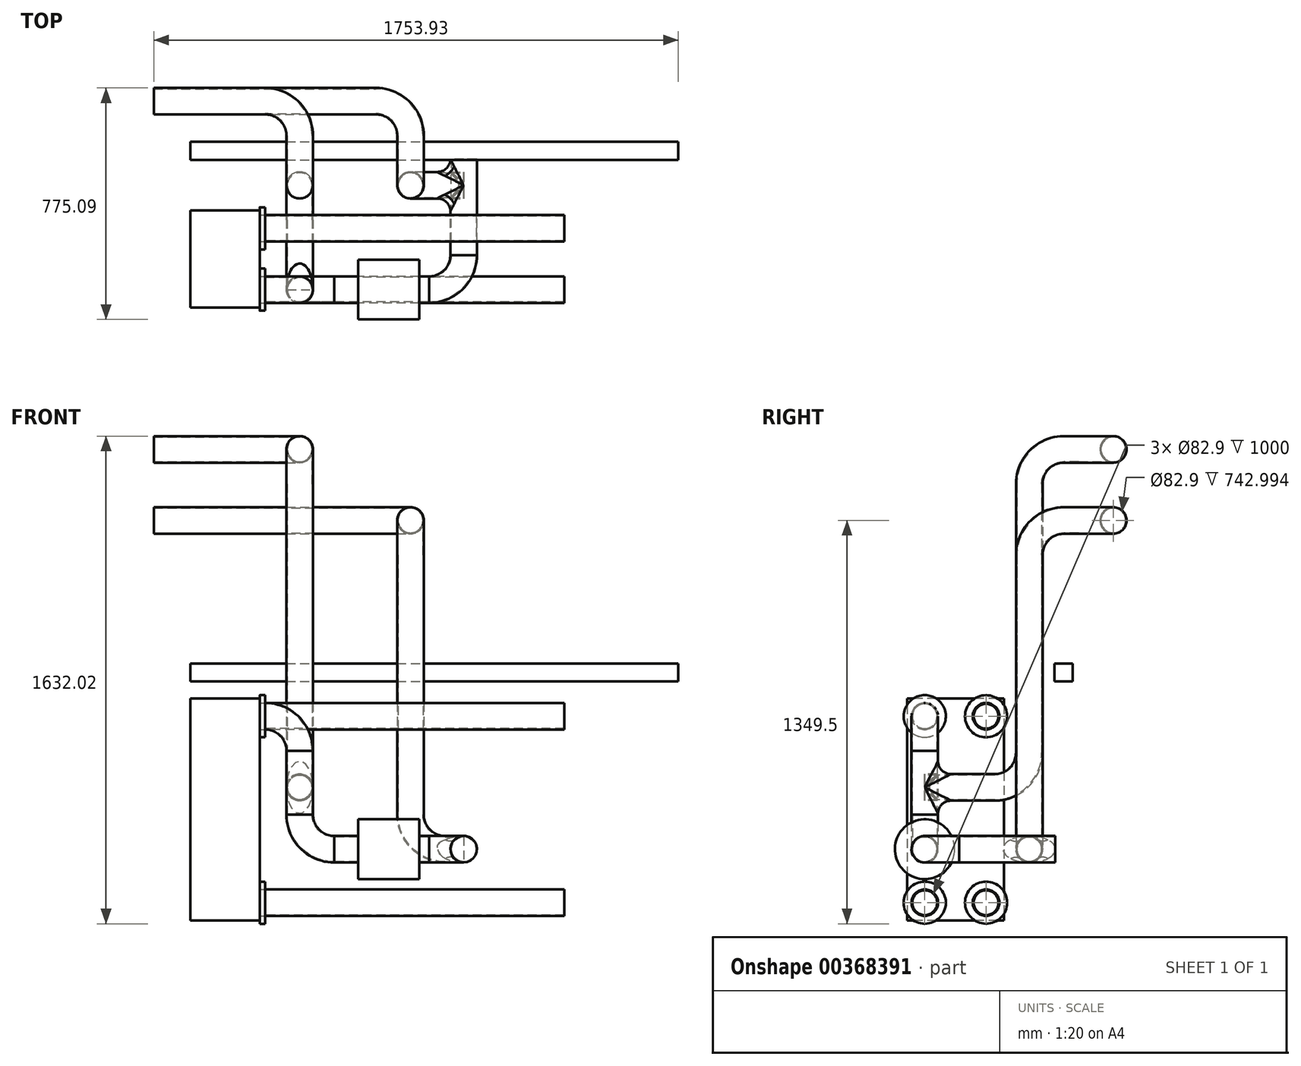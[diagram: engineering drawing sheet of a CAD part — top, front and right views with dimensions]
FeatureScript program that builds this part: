
annotation { "Feature Type Name" : "Feature", "Feature Type Description" : "" }
export const myFeature = defineFeature(function(context is Context, id is Id, definition is map)
    precondition{}
    {
        {
            var Q0;
            Q0=qCreatedBy(makeId("Right.planeOp"),FACE);
            var sketch = newSketch(context, id + "F0", { "sketchPlane" : qUnion([Q0])});
            skLineSegment(sketch, "E0.bottom", {"start": v(162, 371) * mm, "end": v(-162, 371) * mm});
            skLineSegment(sketch, "E0.top", {"start": v(162, -371) * mm, "end": v(-162, -371) * mm});
            skLineSegment(sketch, "E0.left", {"start": v(162, 371) * mm, "end": v(162, -371) * mm});
            skLineSegment(sketch, "E0.right", {"start": v(-162, 371) * mm, "end": v(-162, -371) * mm});
            skPoint(sketch, "E0.middle", {"position": v(0, 0) * mm});
            skLineSegment(sketch, "E1.bottom", {"start": v(102.5, 312) * mm, "end": v(-102.5, 312) * mm, "construction": true});
            skLineSegment(sketch, "E1.top", {"start": v(102.5, -312) * mm, "end": v(-102.5, -312) * mm, "construction": true});
            skLineSegment(sketch, "E1.left", {"start": v(102.5, 312) * mm, "end": v(102.5, -312) * mm, "construction": true});
            skLineSegment(sketch, "E1.right", {"start": v(-102.5, 312) * mm, "end": v(-102.5, -312) * mm, "construction": true});
            skLineSegment(sketch, "E2.bottom", {"start": v(332, 488.24) * mm, "end": v(392, 488.24) * mm});
            skLineSegment(sketch, "E2.top", {"start": v(332, 428.24) * mm, "end": v(392, 428.24) * mm});
            skLineSegment(sketch, "E2.left", {"start": v(332, 488.24) * mm, "end": v(332, 428.24) * mm});
            skLineSegment(sketch, "E2.right", {"start": v(392, 488.24) * mm, "end": v(392, 428.24) * mm});
            skSolve(sketch);
        }
        {
            var Q0;
            Q0 = qSketchRegion(id + "F0", true);
            extrude(context, id + "F1", {"entities" : qUnion([Q0]), "oppositeDirection" : true, "depth" : (232.4 + 18.5) * mm, "hasSecondDirection" : true, "secondDirectionOppositeDirection" : true, "secondDirectionDepth" : 18.5 * mm});
        }
        {
            var Q0;
            Q0=makeQuery(id+"F0.imprint","IMPRINT",FACE,{"disambiguationData":[TD([[makeQuery(id+"F0.imprint","IMPRINT",EDGE,{"derivedFrom":sQuery(id+"F0.wireOp",EDGE,"E0.bottom")}),1.0]])]});
            var sketch = newSketch(context, id + "F2", { "sketchPlane" : qUnion([Q0])});
            skPoint(sketch, "E3.0", {"position": v(-102.5, 312) * mm});
            skPoint(sketch, "E3.1", {"position": v(102.5, 312) * mm});
            skPoint(sketch, "E3.2", {"position": v(102.5, -312) * mm});
            skPoint(sketch, "E3.3", {"position": v(-102.5, -312) * mm});
            skCircle(sketch, "E4", {"center": v(-102.5, 312) * mm, "radius": 70.5 * mm});
            skCircle(sketch, "E5", {"center": v(-102.5, 312) * mm, "radius": 44.45 * mm});
            skCircle(sketch, "E6.0.1.0", {"center": v(-102.5, -312) * mm, "radius": 70.5 * mm});
            skCircle(sketch, "E6.0.1.1", {"center": v(-102.5, -312) * mm, "radius": 44.45 * mm});
            skCircle(sketch, "E6.1.0.0", {"center": v(102.5, 312) * mm, "radius": 70.5 * mm});
            skCircle(sketch, "E6.1.0.1", {"center": v(102.5, 312) * mm, "radius": 44.45 * mm});
            skCircle(sketch, "E6.1.1.0", {"center": v(102.5, -312) * mm, "radius": 70.5 * mm});
            skCircle(sketch, "E6.1.1.1", {"center": v(102.5, -312) * mm, "radius": 44.45 * mm});
            skLineSegment(sketch, "E6.direction1", {"start": v(-102.5, 312) * mm, "end": v(102.5, 312) * mm, "construction": true});
            skLineSegment(sketch, "E6.direction2", {"start": v(-102.5, 312) * mm, "end": v(-102.5, -312) * mm, "construction": true});
            skSolve(sketch);
        }
        {
            var Q0;
            Q0 = qSketchRegion(id + "F2", true);
            extrude(context, id + "F3", {"entities" : qUnion([Q0]), "operationType" : NewBodyOperationType.ADD, "oppositeDirection" : true, "depth" : 18.5 * mm});
        }
        {
            var Q0;
            Q0=makeQuery(id+"F0.imprint","IMPRINT",FACE,{"disambiguationData":[TD([[makeQuery(id+"F0.imprint","IMPRINT",EDGE,{"derivedFrom":sQuery(id+"F0.wireOp",EDGE,"E0.bottom")}),1.0]])]});
            var sketch = newSketch(context, id + "F4", { "sketchPlane" : qUnion([Q0])});
            skPoint(sketch, "E7.0", {"position": v(-102.5, 312) * mm});
            skPoint(sketch, "E7.1", {"position": v(102.5, 312) * mm});
            skPoint(sketch, "E7.2", {"position": v(-102.5, -312) * mm});
            skPoint(sketch, "E7.3", {"position": v(102.5, -312) * mm});
            skCircle(sketch, "E8", {"center": v(-102.5, 312) * mm, "radius": 44.45 * mm});
            skCircle(sketch, "E9.0", {"center": v(-102.5, 312) * mm, "radius": 41.45 * mm});
            skCircle(sketch, "E10.0.1.0", {"center": v(-102.5, -312) * mm, "radius": 44.45 * mm});
            skCircle(sketch, "E10.0.1.1", {"center": v(-102.5, -312) * mm, "radius": 41.45 * mm});
            skCircle(sketch, "E10.1.0.0", {"center": v(102.5, 312) * mm, "radius": 44.45 * mm});
            skCircle(sketch, "E10.1.0.1", {"center": v(102.5, 312) * mm, "radius": 41.45 * mm});
            skCircle(sketch, "E10.1.1.0", {"center": v(102.5, -312) * mm, "radius": 44.45 * mm});
            skCircle(sketch, "E10.1.1.1", {"center": v(102.5, -312) * mm, "radius": 41.45 * mm});
            skLineSegment(sketch, "E10.direction1", {"start": v(-102.5, 312) * mm, "end": v(102.5, 312) * mm, "construction": true});
            skLineSegment(sketch, "E10.direction2", {"start": v(-102.5, 312) * mm, "end": v(-102.5, -312) * mm, "construction": true});
            skSolve(sketch);
        }
        {
            var Q0;
            Q0=makeQuery(id+"F4.imprint","IMPRINT",FACE,{"disambiguationData":[TD([[makeQuery(id+"F4.imprint","IMPRINT",EDGE,{"derivedFrom":sQuery(id+"F4.wireOp",EDGE,"E10.1.0.0")}),1.0]])]});
            var Q1;
            Q1=makeQuery(id+"F4.imprint","IMPRINT",FACE,{"disambiguationData":[TD([[makeQuery(id+"F4.imprint","IMPRINT",EDGE,{"derivedFrom":sQuery(id+"F4.wireOp",EDGE,"E10.0.1.0")}),1.0]])]});
            var Q2;
            Q2=makeQuery(id+"F4.imprint","IMPRINT",FACE,{"disambiguationData":[TD([[makeQuery(id+"F4.imprint","IMPRINT",EDGE,{"derivedFrom":sQuery(id+"F4.wireOp",EDGE,"E10.1.1.0")}),1.0]])]});
            extrude(context, id + "F5", {"entities" : qUnion([Q0, Q1, Q2]), "depth" : 1000 * mm});
        }
        {
            var Q0;
            Q0=sQuery(id+"F4.wireOp",EDGE,"E10.direction1");
            var Q1;
            Q1=sQuery(id+"F4.wireOp",VERTEX,"E7.0");
            cPlane(context, id + "F6", {"entities" : qUnion([Q0, Q1]), "cplaneType" : CPlaneType.LINE_POINT, "offset" : 25 * mm, "width" : 150 * mm, "height" : 150 * mm});
        }
        {
            var Q0;
            Q0=qCreatedBy(id+"F6.planeOp",FACE);
            var sketch = newSketch(context, id + "F7", { "sketchPlane" : qUnion([Q0])});
            skPoint(sketch, "E11.0", {"position": v(0, 312) * mm});
            skLineSegment(sketch, "E12", {"start": v(0.11, 312) * mm, "end": v(0, 312) * mm});
            skLineSegment(sketch, "E13", {"start": v(-115.46, 196.43) * mm, "end": v(-115.46, -17.43) * mm});
            skLineSegment(sketch, "E14", {"start": v(-231.03, -133) * mm, "end": v(-420.26, -133) * mm});
            skPoint(sketch, "E15.visualSharp", {"position": v(-115.46, 312) * mm});
            skArc(sketch, "E15.filletArc", {"start": v(0.11, 312) * mm, "mid": v(-81.6, 278.15) * mm, "end": v(-115.46, 196.43) * mm});
            skPoint(sketch, "E16.visualSharp", {"position": v(-115.46, -133) * mm});
            skArc(sketch, "E16.filletArc", {"start": v(-231.03, -133) * mm, "mid": v(-149.3, -99.15) * mm, "end": v(-115.46, -17.43) * mm});
            skPoint(sketch, "E17", {"position": v(-115.46, 73.93) * mm});
            skLineSegment(sketch, "E18", {"start": v(0.11, 356.45) * mm, "end": v(0.11, 267.55) * mm, "construction": true});
            skLineSegment(sketch, "E19", {"start": v(-71, 196.43) * mm, "end": v(-159.9, 196.43) * mm, "construction": true});
            skPoint(sketch, "E20", {"position": v(0.11, 312) * mm});
            skPoint(sketch, "E21", {"position": v(-115.46, 196.43) * mm});
            skSolve(sketch);
        }
        {
            var Q0;
            Q0=sQuery(id+"F7.wireOp",EDGE,"E13");
            var Q1;
            Q1=sQuery(id+"F7.wireOp",VERTEX,"E16.visualSharp");
            cPlane(context, id + "F8", {"entities" : qUnion([Q0, Q1]), "cplaneType" : CPlaneType.LINE_POINT, "offset" : 25 * mm, "width" : 150 * mm, "height" : 150 * mm});
        }
        {
            var Q0;
            Q0=qCreatedBy(id+"F8.planeOp",FACE);
            var sketch = newSketch(context, id + "F9", { "sketchPlane" : qUnion([Q0])});
            skPoint(sketch, "E22.0", {"position": v(420.26, 102.5) * mm});
            skLineSegment(sketch, "E23", {"start": v(420.26, 102.5) * mm, "end": v(548.38, 102.5) * mm});
            skLineSegment(sketch, "E24", {"start": v(663.95, -13.07) * mm, "end": v(663.95, -334.5) * mm});
            skPoint(sketch, "E25.visualSharp", {"position": v(663.95, 102.5) * mm});
            skArc(sketch, "E25.filletArc", {"start": v(663.95, -13.07) * mm, "mid": v(630.1, 68.65) * mm, "end": v(548.38, 102.5) * mm});
            skPoint(sketch, "E26", {"position": v(663.95, -247) * mm});
            skSolve(sketch);
        }
        {
            var Q0;
            Q0=sQuery(id+"F9.wireOp",EDGE,"E24");
            var Q1;
            Q1=sQuery(id+"F9.wireOp",VERTEX,"E26");
            cPlane(context, id + "F10", {"entities" : qUnion([Q0, Q1]), "cplaneType" : CPlaneType.LINE_POINT, "offset" : 25 * mm, "width" : 150 * mm, "height" : 150 * mm});
        }
        {
            var Q0;
            Q0=qCreatedBy(id+"F10.planeOp",FACE);
            var sketch = newSketch(context, id + "F11", { "sketchPlane" : qUnion([Q0])});
            skPoint(sketch, "E27.0", {"position": v(-663.95, -133) * mm});
            skLineSegment(sketch, "E28", {"start": v(-663.95, -133) * mm, "end": v(-601.7, -133) * mm});
            skLineSegment(sketch, "E29", {"start": v(-486.14, -17.43) * mm, "end": v(-486.14, 226.52) * mm});
            skPoint(sketch, "E30.visualSharp", {"position": v(-486.14, -133) * mm});
            skArc(sketch, "E30.filletArc", {"start": v(-601.7, -133) * mm, "mid": v(-519.99, -99.15) * mm, "end": v(-486.14, -17.43) * mm});
            skSolve(sketch);
        }
        {
            var Q0;
            Q0=sQuery(id+"F11.wireOp",EDGE,"E28");
            var Q1;
            Q1=sQuery(id+"F11.wireOp",VERTEX,"E30.visualSharp");
            cPlane(context, id + "F12", {"entities" : qUnion([Q0, Q1]), "cplaneType" : CPlaneType.LINE_POINT, "offset" : 25 * mm, "width" : 150 * mm, "height" : 150 * mm});
        }
        {
            var Q0;
            Q0=qCreatedBy(id+"F12.planeOp",FACE);
            var sketch = newSketch(context, id + "F13", { "sketchPlane" : qUnion([Q0])});
            skPoint(sketch, "E31.0", {"position": v(-247, 226.52) * mm});
            skLineSegment(sketch, "E32", {"start": v(-247, 226.52) * mm, "end": v(-247, 851.43) * mm});
            skLineSegment(sketch, "E33", {"start": v(-362.57, 967) * mm, "end": v(-387.57, 967) * mm});
            skPoint(sketch, "E34.visualSharp", {"position": v(-247, 967) * mm});
            skArc(sketch, "E34.filletArc", {"start": v(-247, 851.43) * mm, "mid": v(-280.85, 933.15) * mm, "end": v(-362.57, 967) * mm});
            skSolve(sketch);
        }
        {
            var Q0;
            Q0=sQuery(id+"F11.wireOp",EDGE,"E29");
            var Q1;
            Q1=sQuery(id+"F13.wireOp",VERTEX,"E34.visualSharp");
            cPlane(context, id + "F14", {"entities" : qUnion([Q0, Q1]), "cplaneType" : CPlaneType.LINE_POINT, "offset" : 25 * mm, "width" : 150 * mm, "height" : 150 * mm});
        }
        {
            var Q0;
            Q0=qCreatedBy(id+"F14.planeOp",FACE);
            var sketch = newSketch(context, id + "F15", { "sketchPlane" : qUnion([Q0])});
            skPoint(sketch, "E35.0", {"position": v(486.14, 387.57) * mm});
            skLineSegment(sketch, "E36", {"start": v(486.14, 387.57) * mm, "end": v(486.14, 412.57) * mm});
            skLineSegment(sketch, "E37", {"start": v(370.57, 528.14) * mm, "end": v(-372.43, 528.14) * mm});
            skPoint(sketch, "E38.visualSharp", {"position": v(486.14, 528.14) * mm});
            skArc(sketch, "E38.filletArc", {"start": v(486.14, 412.57) * mm, "mid": v(452.29, 494.3) * mm, "end": v(370.57, 528.14) * mm});
            skSolve(sketch);
        }
        {
            var Q0;
            Q0=sQuery(id+"F7.wireOp",EDGE,"E12");
            var Q1;
            Q1=sQuery(id+"F7.wireOp",VERTEX,"E15.visualSharp");
            cPlane(context, id + "F16", {"entities" : qUnion([Q0, Q1]), "cplaneType" : CPlaneType.LINE_POINT, "offset" : 25 * mm, "width" : 150 * mm, "height" : 150 * mm});
        }
        {
            var Q0;
            Q0=qCreatedBy(id+"F16.planeOp",FACE);
            var sketch = newSketch(context, id + "F17", { "sketchPlane" : qUnion([Q0])});
            skPoint(sketch, "E39.0", {"position": v(-102.5, 73.93) * mm});
            skLineSegment(sketch, "E40", {"start": v(-102.5, 73.93) * mm, "end": v(131.43, 73.93) * mm});
            skLineSegment(sketch, "E41", {"start": v(247, 189.5) * mm, "end": v(247, 1089.5) * mm});
            skLineSegment(sketch, "E42", {"start": v(362.57, 1205.07) * mm, "end": v(385.9, 1205.07) * mm});
            skPoint(sketch, "E43.visualSharp", {"position": v(247, 73.93) * mm});
            skArc(sketch, "E43.filletArc", {"start": v(131.43, 73.93) * mm, "mid": v(213.15, 107.78) * mm, "end": v(247, 189.5) * mm});
            skPoint(sketch, "E44.visualSharp", {"position": v(247, 1205.07) * mm});
            skArc(sketch, "E44.filletArc", {"start": v(362.57, 1205.07) * mm, "mid": v(280.85, 1171.22) * mm, "end": v(247, 1089.5) * mm});
            skLineSegment(sketch, "E45", {"start": v(-102.5, -22.36) * mm, "end": v(-102.5, 369.56) * mm, "construction": true});
            skLineSegment(sketch, "E46.bottom", {"start": v(-146.95, 161.43) * mm, "end": v(-58.05, 161.43) * mm, "construction": true});
            skLineSegment(sketch, "E46.top", {"start": v(-146.95, -13.57) * mm, "end": v(-58.05, -13.57) * mm, "construction": true});
            skLineSegment(sketch, "E46.left", {"start": v(-146.95, 161.43) * mm, "end": v(-146.95, -13.57) * mm, "construction": true});
            skLineSegment(sketch, "E46.right", {"start": v(-58.05, 161.43) * mm, "end": v(-58.05, -13.57) * mm, "construction": true});
            skLineSegment(sketch, "E47", {"start": v(-16.95, 118.38) * mm, "end": v(-16.95, 29.48) * mm, "construction": true});
            skPoint(sketch, "E48", {"position": v(-16.95, 73.93) * mm});
            skArc(sketch, "E49", {"start": v(-58.05, 161.43) * mm, "mid": v(-46.13, 131.67) * mm, "end": v(-16.95, 118.38) * mm, "construction": true});
            skArc(sketch, "E50.MirrorCS", {"start": v(-58.05, -13.57) * mm, "mid": v(-46.13, 16.19) * mm, "end": v(-16.95, 29.48) * mm, "construction": true});
            skSolve(sketch);
        }
        {
            var Q0;
            Q0=sQuery(id+"F17.wireOp",EDGE,"E41");
            var Q1;
            Q1=sQuery(id+"F17.wireOp",VERTEX,"E44.visualSharp");
            cPlane(context, id + "F18", {"entities" : qUnion([Q0, Q1]), "cplaneType" : CPlaneType.LINE_POINT, "offset" : 25 * mm, "width" : 150 * mm, "height" : 150 * mm});
        }
        {
            var Q0;
            Q0=qCreatedBy(id+"F18.planeOp",FACE);
            var sketch = newSketch(context, id + "F19", { "sketchPlane" : qUnion([Q0])});
            skPoint(sketch, "E51.0", {"position": v(115.46, 385.9) * mm});
            skLineSegment(sketch, "E52", {"start": v(115.46, 385.9) * mm, "end": v(115.46, 412.57) * mm});
            skLineSegment(sketch, "E53", {"start": v(-0.11, 528.14) * mm, "end": v(-372.43, 528.14) * mm});
            skPoint(sketch, "E54.visualSharp", {"position": v(115.46, 528.14) * mm});
            skArc(sketch, "E54.filletArc", {"start": v(115.46, 412.57) * mm, "mid": v(81.6, 494.3) * mm, "end": v(-0.11, 528.14) * mm});
            skPoint(sketch, "E55.0", {"position": v(-372.43, 528.14) * mm});
            skSolve(sketch);
        }
        {
            var Q0;
            Q0=sQuery(id+"F19.wireOp",EDGE,"E53");
            var Q1;
            Q1=sQuery(id+"F19.wireOp",VERTEX,"E53.end");
            cPlane(context, id + "F20", {"entities" : qUnion([Q0, Q1]), "cplaneType" : CPlaneType.LINE_POINT, "offset" : 25 * mm, "width" : 150 * mm, "height" : 150 * mm});
        }
        {
            var Q0;
            Q0=qCreatedBy(id+"F20.planeOp",FACE);
            var sketch = newSketch(context, id + "F21", { "sketchPlane" : qUnion([Q0])});
            skPoint(sketch, "E56.0", {"position": v(-528.14, 1205.07) * mm});
            skPoint(sketch, "E57.0", {"position": v(-528.14, 967) * mm});
            skCircle(sketch, "E58", {"center": v(-528.14, 967) * mm, "radius": 44.45 * mm});
            skCircle(sketch, "E59.0", {"center": v(-528.14, 967) * mm, "radius": 41.45 * mm});
            skCircle(sketch, "E60", {"center": v(-528.14, 1205.07) * mm, "radius": 44.45 * mm});
            skCircle(sketch, "E61", {"center": v(-528.14, 1205.07) * mm, "radius": 41.45 * mm});
            skSolve(sketch);
        }
        {
            var Q0;
            Q0=qCreatedBy(id+"F16.planeOp",FACE);
            var sketch = newSketch(context, id + "F22", { "sketchPlane" : qUnion([Q0])});
            skPoint(sketch, "E62.0", {"position": v(-102.5, -133) * mm});
            skCircle(sketch, "E63", {"center": v(-102.5, -133) * mm, "radius": 100 * mm});
            skSolve(sketch);
        }
        {
            var Q0;
            Q0=makeQuery(id+"F4.imprint","IMPRINT",FACE,{"disambiguationData":[TD([[makeQuery(id+"F4.imprint","IMPRINT",EDGE,{"derivedFrom":sQuery(id+"F4.wireOp",EDGE,"E8")}),1.0]])]});
            var Q1;
            Q1=sQuery(id+"F7.wireOp",EDGE,"E15.filletArc");
            var Q2;
            Q2=sQuery(id+"F7.wireOp",EDGE,"E13");
            var Q3;
            Q3=sQuery(id+"F7.wireOp",EDGE,"E16.filletArc");
            var Q4;
            Q4=sQuery(id+"F7.wireOp",EDGE,"E14");
            var Q5;
            Q5=sQuery(id+"F9.wireOp",EDGE,"E23");
            var Q6;
            Q6=sQuery(id+"F9.wireOp",EDGE,"E25.filletArc");
            var Q7;
            Q7=sQuery(id+"F9.wireOp",EDGE,"E24");
            sweep(context, id + "F23", {"profiles" : qUnion([Q0]), "path" : qUnion([Q1, Q2, Q3, Q4, Q5, Q6, Q7])});
        }
        {
            var Q0;
            Q0=makeQuery(id+"F21.imprint","IMPRINT",FACE,{"disambiguationData":[TD([[makeQuery(id+"F21.imprint","IMPRINT",EDGE,{"derivedFrom":sQuery(id+"F21.wireOp",EDGE,"E60")}),1.0]])]});
            var Q1;
            Q1=sQuery(id+"F19.wireOp",EDGE,"E53");
            var Q2;
            Q2=sQuery(id+"F19.wireOp",EDGE,"E54.filletArc");
            var Q3;
            Q3=sQuery(id+"F19.wireOp",EDGE,"E52");
            var Q4;
            Q4=sQuery(id+"F17.wireOp",EDGE,"E42");
            var Q5;
            Q5=sQuery(id+"F17.wireOp",EDGE,"E44.filletArc");
            var Q6;
            Q6=sQuery(id+"F17.wireOp",EDGE,"E41");
            var Q7;
            Q7=sQuery(id+"F17.wireOp",EDGE,"E43.filletArc");
            var Q8;
            Q8=sQuery(id+"F17.wireOp",EDGE,"E40");
            sweep(context, id + "F24", {"operationType" : NewBodyOperationType.ADD, "profiles" : qUnion([Q0]), "path" : qUnion([Q1, Q2, Q3, Q4, Q5, Q6, Q7, Q8])});
        }
        {
            var Q0;
            Q0=makeQuery(id+"F21.imprint","IMPRINT",FACE,{"disambiguationData":[TD([[makeQuery(id+"F21.imprint","IMPRINT",EDGE,{"derivedFrom":sQuery(id+"F21.wireOp",EDGE,"E58")}),1.0]])]});
            var Q1;
            Q1=sQuery(id+"F15.wireOp",EDGE,"E37");
            var Q2;
            Q2=sQuery(id+"F15.wireOp",EDGE,"E38.filletArc");
            var Q3;
            Q3=sQuery(id+"F15.wireOp",EDGE,"E36");
            var Q4;
            Q4=sQuery(id+"F13.wireOp",EDGE,"E33");
            var Q5;
            Q5=sQuery(id+"F13.wireOp",EDGE,"E34.filletArc");
            var Q6;
            Q6=sQuery(id+"F13.wireOp",EDGE,"E32");
            var Q7;
            Q7=sQuery(id+"F11.wireOp",EDGE,"E29");
            var Q8;
            Q8=sQuery(id+"F11.wireOp",EDGE,"E30.filletArc");
            var Q9;
            Q9=sQuery(id+"F11.wireOp",EDGE,"E28");
            sweep(context, id + "F25", {"operationType" : NewBodyOperationType.ADD, "profiles" : qUnion([Q0]), "path" : qUnion([Q1, Q2, Q3, Q4, Q5, Q6, Q7, Q8, Q9])});
        }
        {
            var Q0;
            Q0=makeQuery(id+"F24.boolean.opBoolean","INTERSECT",EDGE,{"disambiguationData":[OD(1.0)],"derivedFrom":[makeQuery(id+"F23.opSweep","SWEPT_FACE",FACE,{"disambiguationData":[OSD([sQuery(id+"F4.wireOp",EDGE,"E8"),sQuery(id+"F7.wireOp",EDGE,"E13")])]}),makeQuery(id+"F24.opSweep","SWEPT_FACE",FACE,{"disambiguationData":[OSD([sQuery(id+"F17.wireOp",EDGE,"E40"),sQuery(id+"F21.wireOp",EDGE,"E60")])]})]});
            var Q1;
            Q1=makeQuery(id+"F24.boolean.opBoolean","INTERSECT",EDGE,{"disambiguationData":[OD(0.0)],"derivedFrom":[makeQuery(id+"F23.opSweep","SWEPT_FACE",FACE,{"disambiguationData":[OSD([sQuery(id+"F4.wireOp",EDGE,"E8"),sQuery(id+"F7.wireOp",EDGE,"E13")])]}),makeQuery(id+"F24.opSweep","SWEPT_FACE",FACE,{"disambiguationData":[OSD([sQuery(id+"F17.wireOp",EDGE,"E40"),sQuery(id+"F21.wireOp",EDGE,"E60")])]})]});
            var Q2;
            Q2=makeQuery(id+"F25.boolean.opBoolean","INTERSECT",EDGE,{"disambiguationData":[OD(0.0)],"derivedFrom":[makeQuery(id+"F23.opSweep","SWEPT_FACE",FACE,{"disambiguationData":[OSD([sQuery(id+"F4.wireOp",EDGE,"E8"),sQuery(id+"F9.wireOp",EDGE,"E24")])]}),makeQuery(id+"F25.opSweep","SWEPT_FACE",FACE,{"disambiguationData":[OSD([sQuery(id+"F11.wireOp",EDGE,"E28"),sQuery(id+"F21.wireOp",EDGE,"E58")])]})]});
            var Q3;
            Q3=makeQuery(id+"F25.boolean.opBoolean","INTERSECT",EDGE,{"disambiguationData":[OD(1.0)],"derivedFrom":[makeQuery(id+"F23.opSweep","SWEPT_FACE",FACE,{"disambiguationData":[OSD([sQuery(id+"F4.wireOp",EDGE,"E8"),sQuery(id+"F9.wireOp",EDGE,"E24")])]}),makeQuery(id+"F25.opSweep","SWEPT_FACE",FACE,{"disambiguationData":[OSD([sQuery(id+"F11.wireOp",EDGE,"E28"),sQuery(id+"F21.wireOp",EDGE,"E58")])]})]});
            fillet(context, id + "F26", {"entities" : qUnion([Q0, Q1, Q2, Q3]), "radius" : 43 * mm, "tangentPropagation" : true, "allowEdgeOverflow" : false});
        }
        {
            var Q0;
            Q0=makeQuery(id+"F22.imprint","IMPRINT",FACE,{"disambiguationData":[TD([[makeQuery(id+"F22.imprint","IMPRINT",EDGE,{"derivedFrom":sQuery(id+"F22.wireOp",EDGE,"E63")}),1.0]])]});
            extrude(context, id + "F27", {"entities" : qUnion([Q0]), "operationType" : NewBodyOperationType.ADD, "depth" : 400 * mm, "hasSecondDirection" : true, "secondDirectionOppositeDirection" : false, "secondDirectionDepth" : 195 * mm});
        }
        {
            var Q0;
            Q0=makeQuery(id+"F1.opExtrude","CAP_FACE",FACE,{"disambiguationData":[OSD([sQuery(id+"F0.wireOp",EDGE,"E2.bottom"),sQuery(id+"F0.wireOp",EDGE,"E2.top"),sQuery(id+"F0.wireOp",EDGE,"E2.left"),sQuery(id+"F0.wireOp",EDGE,"E2.right")])],"isStart":true});
            extrude(context, id + "F28", {"entities" : qUnion([Q0]), "operationType" : NewBodyOperationType.ADD, "depth" : 1400 * mm});
        }
    });
